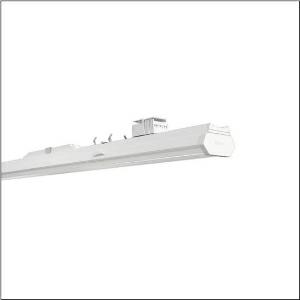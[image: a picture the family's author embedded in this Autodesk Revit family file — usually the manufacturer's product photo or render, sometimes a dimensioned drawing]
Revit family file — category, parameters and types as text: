
# Revit family: licross_11_protected_ho_51tp12mn4f5m
name_source: partatom
category: Lighting Fixtures
units: mm (PartAtom-declared; Revit-internal decimal feet)

## family parameters
Cut with Voids When Loaded = No
Host = Face
Light Source = No
Part Type = Normal
Room Calculation Point = No
Round Connector Dimension = Use Diameter
Shared = No

## types (1)
- --- (1 x LED, 15820 lm, 87.4 W, 4000K)
    Apparent Load = 87 VA
    CIE Flux Codes = 70 91 97 98 100
    Color Rendering = 80
    Color Temperature = 4000K
    Default Elevation = 1800 mm
    Description = Licross 11 Protected HO, luminaire insert, of sheet steel, galvanised, coil coated, white, length: 1.500mm, width: 90mm, height: 101mm, LED rated luminous flux: 15.820lm, light colour: 840, SDCM (Standard Deviation of Colour Matching)MacAdam ≤ 2 SDCM (initial), control gear: ON/OFF Multilumen, with plug, 3-pole, with phase selection, mains connection: 220..240V, AC, 50/60Hz, rated input power: 87W, internal wiring halogen-free, primary light control with lens, of plastic, primary optical cover: cover, of PMMA, light emission: direct distribution, primary light characteristic: symmetric, protection rating (complete): IP64, insulation class (complete): insulation class I (protective earthing), certification: CE, ENEC, VDE, UKCA, protection symbol: D if used in an environment with conductive dust loads with corresponding accessories, impact resistance: IK06, permissible ambient temperature for indoor applications: -35..+35°C, corresponds to IFS (International Featured Standards) requirements for safety and quality in the food industry, reducing of maximum allowable ambient temperature of 5°C with ceiling mounting, LABS conformity tested according to VDMA 24364:2018-05, The light source and the operating device comply with the requirements of the Ecodesign Regulation (EU) 2019/2020 and are replaceable in accordance with this regulation, packaging unit: 1 piece
    Height = 92 mm
    Lamp = 1 x LED
    Lamp Light Flux = 15820 lm
    Lamp Power = 87.4 W
    Lamp count = 1
    Length = 1500 mm
    Luminous efficacy = 181 lm/W
    Manufacturer = Siteco
    ModVariant = No
    Model = 51TP12MN4F5M
    Mounting Place = Ceiling
    Mounting Type = Pendant
    Number of Poles = 1
    OnlyDefault = Yes
    Power Factor = 1
    Product Name = Licross 11 Protected HO
    Product group = luminaire insert | ceiling pendant
    ProductGroupID = 901
    Protection Class = Protection class I
    Protection Degree = IP 64
    RLX_Detail_Level = 1
    RLX_Emergency_Light_Flux = 0 lm
    RLX_Emergency_Type = 0
    RLX_Emergency_Type_DB = No
    RlxData = <blob elided: 22353 chars, md5=a786de1d>
    Socket = socket
    Standby Power = 0 W
    System Light Flux = 15820 lm
    System Power = 87 W
    Type Comments = factory setting: luminous flux: 100 % | (A | C | E) | 203 mA
    Type Image = l_1256148.jpg
    URL = http://relux.com
    VarID = @adj_090489
    Voltage = 0 V
    Weight = 0.00 kg
    Width = 88 mm

## geometry (parser evidence)
native form markers: Blend x4, Sweep x12
no freeform markers — native parametric forms only
